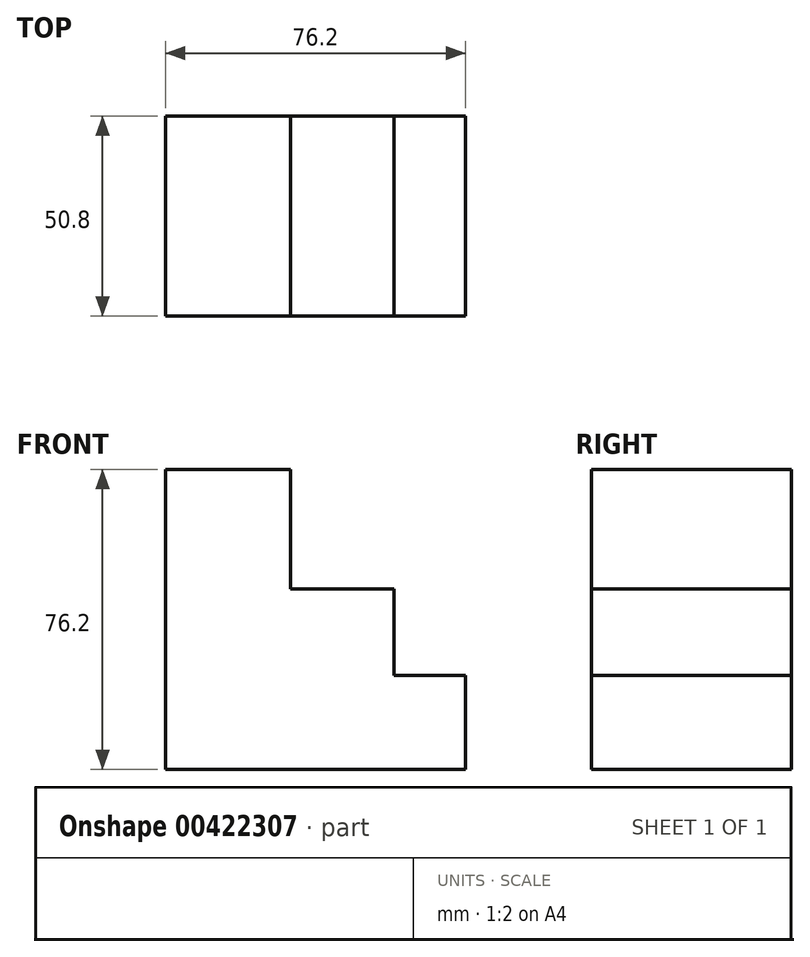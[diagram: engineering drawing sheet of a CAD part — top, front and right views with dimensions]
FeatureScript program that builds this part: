
annotation { "Feature Type Name" : "Feature", "Feature Type Description" : "" }
export const myFeature = defineFeature(function(context is Context, id is Id, definition is map)
    precondition{}
    {
        {
            var Q0;
            Q0=qCreatedBy(makeId("Front.planeOp"),FACE);
            var sketch = newSketch(context, id + "F0", { "sketchPlane" : qUnion([Q0])});
            skPoint(sketch, "E0.start.orphan", {"position": v(-35.94, 67.67) * mm});
            skPoint(sketch, "E1.start.orphan", {"position": v(-16.55, 20.72) * mm});
            skPoint(sketch, "E2.start.orphan", {"position": v(-35.94, -16.3) * mm});
            skPoint(sketch, "E3.end.orphan", {"position": v(6.65, 20.72) * mm});
            skLineSegment(sketch, "E4", {"start": v(-55.64, -28.75) * mm, "end": v(20.56, -28.75) * mm});
            skLineSegment(sketch, "E5", {"start": v(-55.64, -28.75) * mm, "end": v(-55.64, 47.45) * mm});
            skLineSegment(sketch, "E6", {"start": v(-55.64, 47.45) * mm, "end": v(-23.84, 47.45) * mm});
            skLineSegment(sketch, "E7", {"start": v(-23.84, 47.45) * mm, "end": v(-23.84, 17.09) * mm});
            skLineSegment(sketch, "E8", {"start": v(-23.84, 17.09) * mm, "end": v(2.38, 17.09) * mm});
            skLineSegment(sketch, "E9", {"start": v(2.38, 17.09) * mm, "end": v(2.38, -4.9) * mm});
            skLineSegment(sketch, "E10", {"start": v(2.38, -4.9) * mm, "end": v(20.56, -4.9) * mm});
            skLineSegment(sketch, "E11", {"start": v(20.56, -4.9) * mm, "end": v(20.56, -28.75) * mm});
            skSolve(sketch);
        }
        {
            var Q0;
            Q0=makeQuery(id+"F0.imprint","IMPRINT",FACE,{"disambiguationData":[TD([[makeQuery(id+"F0.imprint","IMPRINT",EDGE,{"derivedFrom":sQuery(id+"F0.wireOp",EDGE,"E4")}),1.0]])]});
            extrude(context, id + "F1", {"entities" : qUnion([Q0]), "depth" : 50.8 * mm});
        }
    });
